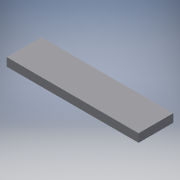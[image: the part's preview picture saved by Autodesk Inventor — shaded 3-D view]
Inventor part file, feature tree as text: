
AUTODESK INVENTOR PART (.ipt)
format: ipt  version: 2016 (Build 200138000, 138)  size: 87,040 bytes
history: native  units: in
note: dims shown in document units (in); Inventor stores cm internally (conversion verified against a paired STEP export)
features: extrude x1, sketch x1
ambient origin geometry x8: Origin, YZ Plane, XZ Plane, XY Plane, X Axis, Y Axis, Z Axis, Center Point
bodies: Solid1 (feature_tree)
feature tree (2):
  extrude  "Extrusion1"  Depth=2.0in
  sketch  "Sketch1"  dims[d0=0.525in d1=2.0in d2=0.125in d3=0.0in]
